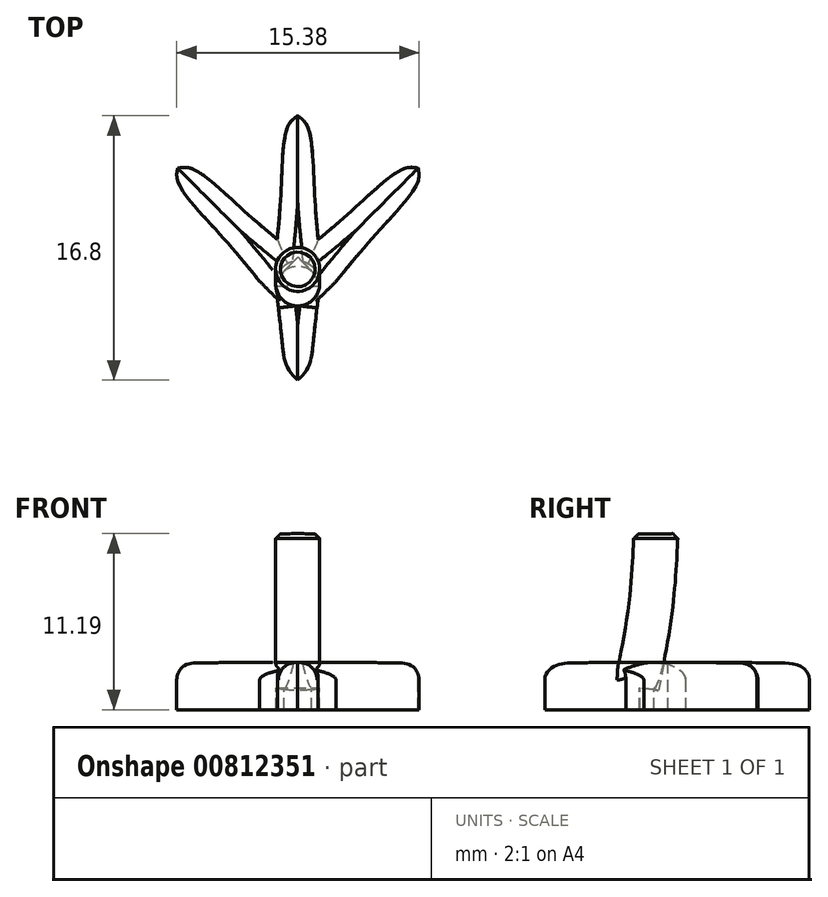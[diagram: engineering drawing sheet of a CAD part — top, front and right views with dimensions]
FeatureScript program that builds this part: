
annotation { "Feature Type Name" : "Feature", "Feature Type Description" : "" }
export const myFeature = defineFeature(function(context is Context, id is Id, definition is map)
    precondition{}
    {
        {
            var Q0;
            Q0=qCreatedBy(makeId("Right.planeOp"),FACE);
            var sketch = newSketch(context, id + "F0", { "sketchPlane" : qUnion([Q0])});
            skPoint(sketch, "E0", {"position": v(40.6, 29.15) * mm});
            skPoint(sketch, "E1", {"position": v(0, -11.44) * mm});
            skSolve(sketch);
        }
        {
            var Q0;
            Q0=qCreatedBy(makeId("Right.planeOp"),FACE);
            var sketch = newSketch(context, id + "F1", { "sketchPlane" : qUnion([Q0])});
            skFitSpline(sketch, "E2", {"points": [v(2.4, 1.18) * mm, v(2, -3.82) * mm, v(1.18, -8.57) * mm], "startDerivative": vector(-0.54, -12.5) * mm, "endDerivative": vector(-1.8, -9.53) * mm});
            skSolve(sketch);
        }
        {
            var Q0;
            Q0=qCreatedBy(makeId("Top.planeOp"),FACE);
            var sketch = newSketch(context, id + "F2", { "sketchPlane" : qUnion([Q0])});
            skCircle(sketch, "E3", {"center": v(0, 2.4) * mm, "radius": 1.4 * mm});
            skSolve(sketch);
        }
        {
            var Q0;
            Q0 = qSketchRegion(id + "F2", true);
            var Q1;
            Q1 = qConstructionFilter(qBodyType(qCreatedBy(id + "F1" ,EDGE), BodyType.WIRE), ConstructionObject.NO);
            sweep(context, id + "F3", {"profiles" : qUnion([Q0]), "path" : qUnion([Q1])});
        }
        {
            var Q0;
            Q0=qCreatedBy(makeId("Top.planeOp"),FACE);
            cPlane(context, id + "F4", {"entities" : qUnion([Q0]), "cplaneType" : CPlaneType.OFFSET, "offset" : 7 * mm, "oppositeDirection" : true, "width" : 150 * mm, "height" : 150 * mm});
        }
        {
            var Q0;
            Q0=qCreatedBy(id+"F4.planeOp",FACE);
            var sketch = newSketch(context, id + "F5", { "sketchPlane" : qUnion([Q0])});
            skPoint(sketch, "E4", {"position": v(0, 12.2) * mm});
            skFitSpline(sketch, "E5", {"points": [v(-1.4, 3.43) * mm, v(-1.06, 7.45) * mm, v(-0.64, 11.48) * mm, v(0, 12.2) * mm], "startDerivative": vector(1, 9.44) * mm, "endDerivative": vector(3.65, 2.54) * mm});
            skFitSpline(sketch, "E6.MirrorCS", {"points": [v(1.4, 3.43) * mm, v(1.06, 7.45) * mm, v(0.64, 11.48) * mm, v(0, 12.2) * mm], "startDerivative": vector(-1, 9.44) * mm, "endDerivative": vector(-3.65, 2.54) * mm});
            skPoint(sketch, "E7.center", {"position": v(0, 0) * mm});
            skLineSegment(sketch, "E7.anchor1", {"start": v(0, 0) * mm, "end": v(-0.38, 0) * mm, "construction": true});
            skFitSpline(sketch, "E8", {"points": [v(-1.4, 1.55) * mm, v(-1.04, 0.44) * mm, v(-0.38, 0) * mm], "startDerivative": vector(0.45, -2.3) * mm, "endDerivative": vector(1.62, -0.75) * mm});
            skFitSpline(sketch, "E9.MirrorCS", {"points": [v(1.4, 1.55) * mm, v(1.04, 0.44) * mm, v(0.38, 0) * mm], "startDerivative": vector(-0.45, -2.3) * mm, "endDerivative": vector(-1.62, -0.75) * mm});
            skLineSegment(sketch, "E10", {"start": v(-1.4, 1.55) * mm, "end": v(-1.4, 3.43) * mm});
            skLineSegment(sketch, "E11", {"start": v(1.4, 1.55) * mm, "end": v(1.4, 3.43) * mm});
            skLineSegment(sketch, "E12", {"start": v(-0.38, 0) * mm, "end": v(0.38, 0) * mm});
            skFitSpline(sketch, "E13", {"points": [v(0.46, 3.66) * mm, v(3.55, 6.26) * mm, v(6.7, 8.81) * mm, v(7.65, 8.87) * mm], "startDerivative": vector(7.38, 5.97) * mm, "endDerivative": vector(4.37, -0.79) * mm});
            skFitSpline(sketch, "E14.MirrorCS", {"points": [v(2.44, 1.68) * mm, v(5.04, 4.77) * mm, v(7.6, 7.9) * mm, v(7.65, 8.87) * mm], "startDerivative": vector(5.97, 7.38) * mm, "endDerivative": vector(-0.79, 4.37) * mm});
            skLineSegment(sketch, "E15.anchor1", {"start": v(-0.97, 0.24) * mm, "end": v(-1.25, 0.52) * mm, "construction": true});
            skFitSpline(sketch, "E16", {"points": [v(-0.87, 2.33) * mm, v(-1.4, 1.3) * mm, v(-1.25, 0.52) * mm], "startDerivative": vector(-1.32, -1.95) * mm, "endDerivative": vector(0.62, -1.68) * mm});
            skFitSpline(sketch, "E17.MirrorCS", {"points": [v(1.11, 0.35) * mm, v(0.07, -0.17) * mm, v(-0.7, -0.03) * mm], "startDerivative": vector(-1.95, -1.32) * mm, "endDerivative": vector(-1.68, 0.62) * mm});
            skLineSegment(sketch, "E18", {"start": v(-0.87, 2.33) * mm, "end": v(0.46, 3.66) * mm});
            skLineSegment(sketch, "E19", {"start": v(1.11, 0.35) * mm, "end": v(2.44, 1.68) * mm});
            skLineSegment(sketch, "E20", {"start": v(-1.25, 0.52) * mm, "end": v(-0.7, -0.03) * mm});
            skFitSpline(sketch, "E21", {"points": [v(-2.42, 1.67) * mm, v(-5.02, 4.76) * mm, v(-7.57, 7.9) * mm, v(-7.63, 8.87) * mm], "startDerivative": vector(-5.97, 7.38) * mm, "endDerivative": vector(0.79, 4.37) * mm});
            skFitSpline(sketch, "E22.MirrorCS", {"points": [v(-0.44, 3.65) * mm, v(-3.53, 6.26) * mm, v(-6.67, 8.81) * mm, v(-7.63, 8.87) * mm], "startDerivative": vector(-7.38, 5.97) * mm, "endDerivative": vector(-4.37, -0.79) * mm});
            skLineSegment(sketch, "E23.anchor1", {"start": v(1, 0.24) * mm, "end": v(0.72, -0.03) * mm, "construction": true});
            skFitSpline(sketch, "E24", {"points": [v(-1.1, 0.35) * mm, v(-0.05, -0.18) * mm, v(0.72, -0.03) * mm], "startDerivative": vector(1.95, -1.32) * mm, "endDerivative": vector(1.68, 0.62) * mm});
            skFitSpline(sketch, "E25.MirrorCS", {"points": [v(0.89, 2.33) * mm, v(1.41, 1.29) * mm, v(1.27, 0.51) * mm], "startDerivative": vector(1.32, -1.95) * mm, "endDerivative": vector(-0.62, -1.68) * mm});
            skLineSegment(sketch, "E26", {"start": v(-1.1, 0.35) * mm, "end": v(-2.42, 1.67) * mm});
            skLineSegment(sketch, "E27", {"start": v(0.89, 2.33) * mm, "end": v(-0.44, 3.65) * mm});
            skLineSegment(sketch, "E28", {"start": v(0.72, -0.03) * mm, "end": v(1.27, 0.51) * mm});
            skSolve(sketch);
        }
        {
            var Q0;
            Q0 = qSketchRegion(id + "F5", true);
            extrude(context, id + "F6", {"entities" : qUnion([Q0]), "operationType" : NewBodyOperationType.ADD, "oppositeDirection" : true, "depth" : 3 * mm, "offsetDistance" : 25 * mm});
        }
        {
            var Q0;
            Q0=qCreatedBy(id+"F4.planeOp",FACE);
            var sketch = newSketch(context, id + "F7", { "sketchPlane" : qUnion([Q0])});
            skLineSegment(sketch, "E29.bottom", {"start": v(-1.4, 1.4) * mm, "end": v(1.4, 1.4) * mm});
            skPoint(sketch, "E30", {"position": v(0, 1.4) * mm});
            skFitSpline(sketch, "E31", {"points": [v(-1.4, 1.4) * mm, v(-1.01, -1.96) * mm, v(-0.69, -3.73) * mm, v(0, -4.6) * mm], "startDerivative": vector(1.01, -8.2) * mm, "endDerivative": vector(3.16, -3.11) * mm});
            skFitSpline(sketch, "E32.MirrorCS", {"points": [v(1.4, 1.4) * mm, v(1.01, -1.96) * mm, v(0.69, -3.73) * mm, v(0, -4.6) * mm], "startDerivative": vector(-1.01, -8.2) * mm, "endDerivative": vector(-3.16, -3.11) * mm});
            skSolve(sketch);
        }
        {
            var Q0;
            Q0 = qSketchRegion(id + "F7", true);
            extrude(context, id + "F8", {"entities" : qUnion([Q0]), "operationType" : NewBodyOperationType.ADD, "oppositeDirection" : true, "depth" : 3 * mm, "offsetDistance" : 25 * mm});
        }
        {
            var Q0;
            Q0=makeQuery(id+"F6.opExtrude","CAP_EDGE",EDGE,{"disambiguationData":[OSD([sQuery(id+"F5.wireOp",EDGE,"E21")])],"isStart":true});
            var Q1;
            Q1=makeQuery(id+"F6.opExtrude","CAP_EDGE",EDGE,{"disambiguationData":[OSD([sQuery(id+"F5.wireOp",EDGE,"E14.MirrorCS")])],"isStart":true});
            var Q2;
            Q2=makeQuery(id+"F6.opExtrude","CAP_EDGE",EDGE,{"disambiguationData":[OSD([sQuery(id+"F5.wireOp",EDGE,"E22.MirrorCS")])],"isStart":true});
            var Q3;
            Q3=makeQuery(id+"F6.opExtrude","CAP_EDGE",EDGE,{"disambiguationData":[OSD([sQuery(id+"F5.wireOp",EDGE,"E5")])],"isStart":true});
            var Q4;
            Q4=makeQuery(id+"F6.opExtrude","CAP_EDGE",EDGE,{"disambiguationData":[OSD([sQuery(id+"F5.wireOp",EDGE,"E6.MirrorCS")])],"isStart":true});
            var Q5;
            Q5=makeQuery(id+"F6.opExtrude","CAP_EDGE",EDGE,{"disambiguationData":[OSD([sQuery(id+"F5.wireOp",EDGE,"E13")])],"isStart":true});
            fillet(context, id + "F9", {"entities" : qUnion([Q0, Q1, Q2, Q3, Q4, Q5]), "radius" : 1.1 * mm, "tangentPropagation" : true, "allowEdgeOverflow" : false});
        }
        {
            var Q0;
            Q0=makeQuery(id+"F8.opExtrude","CAP_EDGE",EDGE,{"disambiguationData":[OSD([sQuery(id+"F7.wireOp",EDGE,"E31")])],"isStart":true});
            var Q1;
            Q1=makeQuery(id+"F8.opExtrude","CAP_EDGE",EDGE,{"disambiguationData":[OSD([sQuery(id+"F7.wireOp",EDGE,"E32.MirrorCS")])],"isStart":true});
            fillet(context, id + "F10", {"entities" : qUnion([Q0, Q1]), "radius" : 1.1 * mm, "tangentPropagation" : true, "allowEdgeOverflow" : false});
        }
        {
            var Q0;
            Q0=makeQuery(id+"F3.opSweep","CAP_EDGE",EDGE,{"disambiguationData":[OSD([sQuery(id+"F1.wireOp",VERTEX,"E2.start"),sQuery(id+"F2.wireOp",EDGE,"E3")])],"isStart":false});
            chamfer(context, id + "F11", {"entities" : qUnion([Q0]), "width" : 0.3 * mm, "tangentPropagation" : true});
        }
    });
